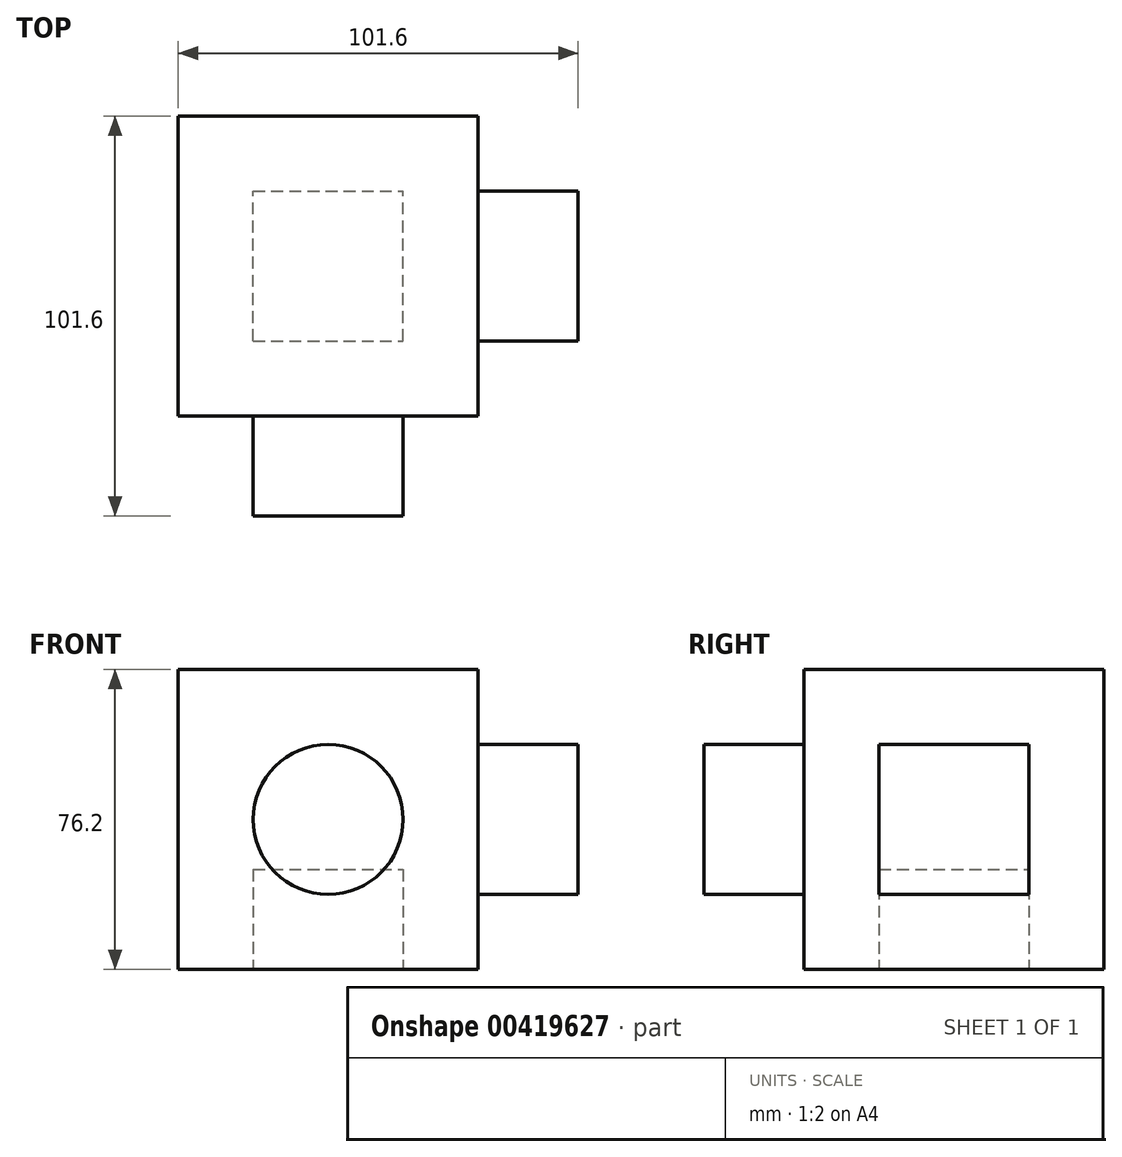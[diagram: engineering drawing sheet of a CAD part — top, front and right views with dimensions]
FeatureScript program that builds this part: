
annotation { "Feature Type Name" : "Feature", "Feature Type Description" : "" }
export const myFeature = defineFeature(function(context is Context, id is Id, definition is map)
    precondition{}
    {
        {
            var Q0;
            Q0=qCreatedBy(makeId("Front.planeOp"),FACE);
            var sketch = newSketch(context, id + "F0", { "sketchPlane" : qUnion([Q0])});
            skLineSegment(sketch, "E0", {"start": v(0, 0) * mm, "end": v(-76.2, 0) * mm});
            skLineSegment(sketch, "E1", {"start": v(-76.2, 0) * mm, "end": v(-76.2, 76.2) * mm});
            skLineSegment(sketch, "E2", {"start": v(-76.2, 76.2) * mm, "end": v(0, 76.2) * mm});
            skLineSegment(sketch, "E3", {"start": v(0, 76.2) * mm, "end": v(0, 0) * mm});
            skSolve(sketch);
        }
        {
            var Q0;
            Q0 = qSketchRegion(id + "F0", true);
            extrude(context, id + "F1", {"entities" : qUnion([Q0]), "depth" : 76.2 * mm});
        }
        {
            var Q0;
            Q0=makeQuery(id+"F1.opExtrude","CAP_FACE",FACE,{"disambiguationData":[OSD([sQuery(id+"F0.wireOp",EDGE,"E0"),sQuery(id+"F0.wireOp",EDGE,"E1"),sQuery(id+"F0.wireOp",EDGE,"E2"),sQuery(id+"F0.wireOp",EDGE,"E3")])],"isStart":false});
            var sketch = newSketch(context, id + "F2", { "sketchPlane" : qUnion([Q0])});
            skCircle(sketch, "E4", {"center": v(-38.1, 38.1) * mm, "radius": 19.05 * mm});
            skLineSegment(sketch, "E5", {"start": v(-38.1, 38.1) * mm, "end": v(-76.2, 38.1) * mm});
            skLineSegment(sketch, "E6", {"start": v(-76.2, 38.1) * mm, "end": v(-38.1, 38.1) * mm});
            skLineSegment(sketch, "E7", {"start": v(-38.1, 38.1) * mm, "end": v(-38.1, 76.2) * mm});
            skSolve(sketch);
        }
        {
            var Q0;
            {var subQ0=sQuery(id+"F2.wireOp",EDGE,"E6");var subQ1=sQuery(id+"F2.wireOp",EDGE,"E4");var subQ2=makeQuery(id+"F2.imprint","INTERSECT",VERTEX,{"derivedFrom":[subQ1,subQ0]});Q0=makeQuery(id+"F2.imprint","IMPRINT",FACE,{"disambiguationData":[TD([[makeQuery(id+"F2.imprint","IMPRINT",EDGE,{"disambiguationData":[TD([[subQ2,-1.0]])],"derivedFrom":subQ1}),1.0]])]});}
            var Q1;
            {var subQ0=sQuery(id+"F2.wireOp",EDGE,"E6");var subQ1=sQuery(id+"F2.wireOp",EDGE,"E4");var subQ2=makeQuery(id+"F2.imprint","INTERSECT",VERTEX,{"derivedFrom":[subQ1,subQ0]});Q1=makeQuery(id+"F2.imprint","IMPRINT",FACE,{"disambiguationData":[TD([[makeQuery(id+"F2.imprint","IMPRINT",EDGE,{"disambiguationData":[TD([[subQ2,1.0]])],"derivedFrom":subQ1}),1.0]])]});}
            extrude(context, id + "F3", {"entities" : qUnion([Q0, Q1]), "operationType" : NewBodyOperationType.ADD, "depth" : 25.4 * mm});
        }
        {
            var Q0;
            Q0=makeQuery(id+"F1.opExtrude","SWEPT_FACE",FACE,{"disambiguationData":[OSD([sQuery(id+"F0.wireOp",EDGE,"E3")])]});
            var sketch = newSketch(context, id + "F4", { "sketchPlane" : qUnion([Q0])});
            skLineSegment(sketch, "E8.bottom", {"start": v(-57.15, 57.15) * mm, "end": v(-19.05, 57.15) * mm});
            skLineSegment(sketch, "E8.top", {"start": v(-57.15, 19.05) * mm, "end": v(-19.05, 19.05) * mm});
            skLineSegment(sketch, "E8.left", {"start": v(-57.15, 57.15) * mm, "end": v(-57.15, 19.05) * mm});
            skLineSegment(sketch, "E8.right", {"start": v(-19.05, 57.15) * mm, "end": v(-19.05, 19.05) * mm});
            skLineSegment(sketch, "E9", {"start": v(-19.05, 57.15) * mm, "end": v(0, 57.15) * mm});
            skLineSegment(sketch, "E10", {"start": v(0, 57.15) * mm, "end": v(-19.05, 57.15) * mm});
            skLineSegment(sketch, "E11", {"start": v(-19.05, 76.2) * mm, "end": v(-19.05, 57.15) * mm});
            skSolve(sketch);
        }
        {
            var Q0;
            Q0=makeQuery(id+"F4.imprint","IMPRINT",FACE,{"disambiguationData":[TD([[makeQuery(id+"F4.imprint","IMPRINT",EDGE,{"derivedFrom":sQuery(id+"F4.wireOp",EDGE,"E8.bottom")}),-1.0]])]});
            extrude(context, id + "F5", {"entities" : qUnion([Q0]), "operationType" : NewBodyOperationType.ADD, "depth" : 25.4 * mm});
        }
        {
            var Q0;
            Q0=makeQuery(id+"F1.opExtrude","SWEPT_FACE",FACE,{"disambiguationData":[OSD([sQuery(id+"F0.wireOp",EDGE,"E0")])]});
            var sketch = newSketch(context, id + "F6", { "sketchPlane" : qUnion([Q0])});
            skLineSegment(sketch, "E12.bottom", {"start": v(-57.15, 57.15) * mm, "end": v(-19.05, 57.15) * mm});
            skLineSegment(sketch, "E12.top", {"start": v(-57.15, 19.05) * mm, "end": v(-19.05, 19.05) * mm});
            skLineSegment(sketch, "E12.left", {"start": v(-57.15, 57.15) * mm, "end": v(-57.15, 19.05) * mm});
            skLineSegment(sketch, "E12.right", {"start": v(-19.05, 57.15) * mm, "end": v(-19.05, 19.05) * mm});
            skSolve(sketch);
        }
        {
            var Q0;
            Q0=makeQuery(id+"F6.imprint","IMPRINT",FACE,{"disambiguationData":[TD([[makeQuery(id+"F6.imprint","IMPRINT",EDGE,{"derivedFrom":sQuery(id+"F6.wireOp",EDGE,"E12.bottom")}),-1.0]])]});
            extrude(context, id + "F7", {"entities" : qUnion([Q0]), "operationType" : NewBodyOperationType.REMOVE, "oppositeDirection" : true, "depth" : 25.4 * mm});
        }
    });
